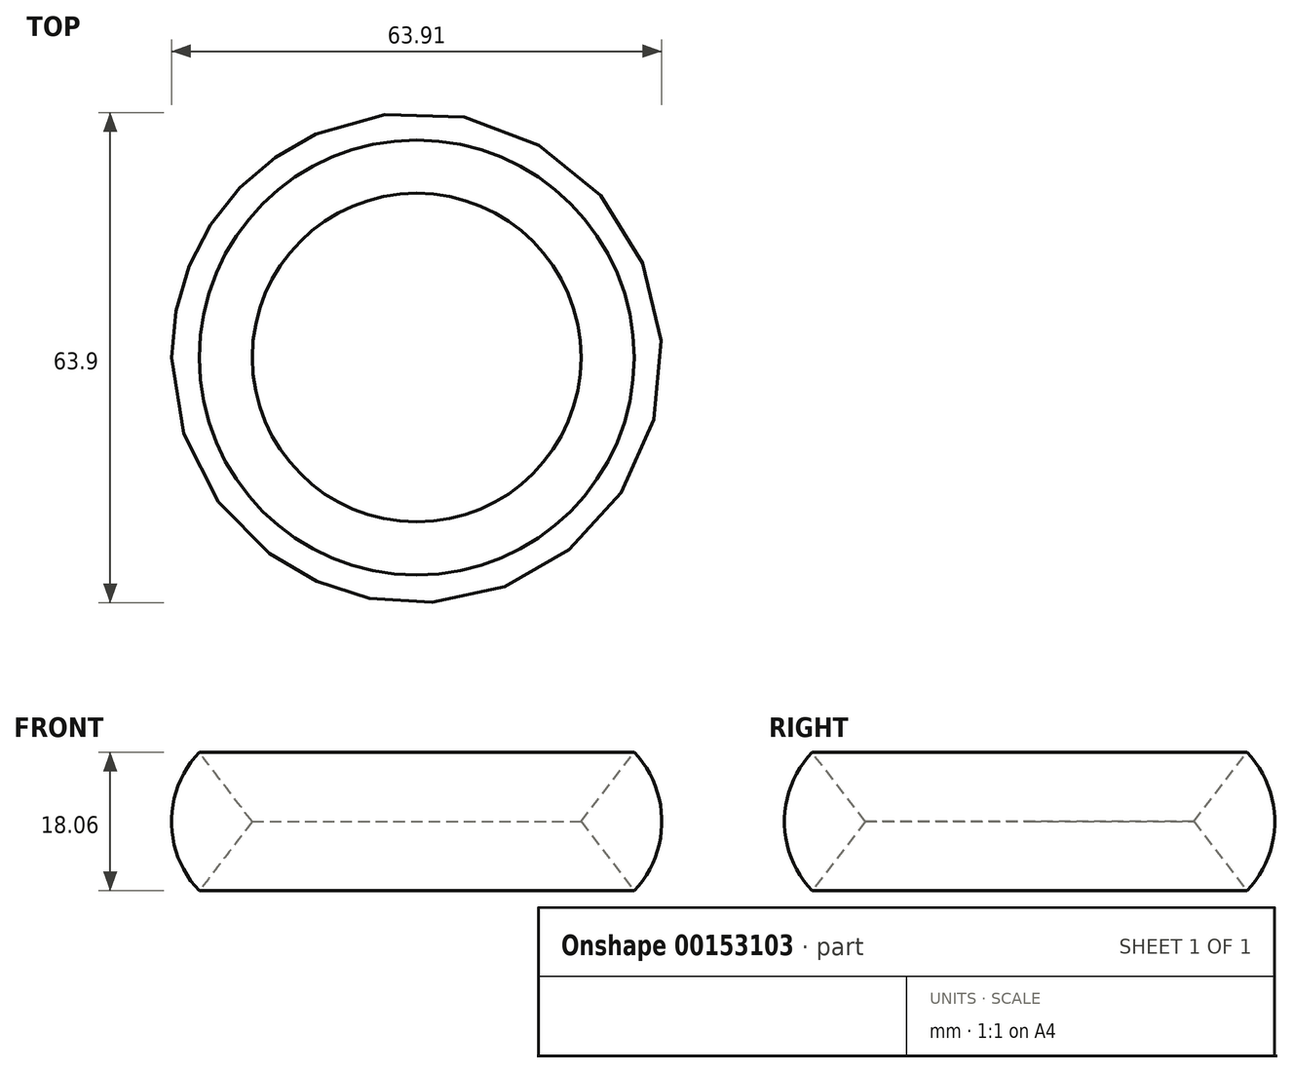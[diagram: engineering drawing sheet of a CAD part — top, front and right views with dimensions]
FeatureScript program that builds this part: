
annotation { "Feature Type Name" : "Feature", "Feature Type Description" : "" }
export const myFeature = defineFeature(function(context is Context, id is Id, definition is map)
    precondition{}
    {
        {
            var Q0;
            Q0=qCreatedBy(makeId("Front.planeOp"),FACE);
            var sketch = newSketch(context, id + "F0", { "sketchPlane" : qUnion([Q0])});
            skLineSegment(sketch, "E0", {"start": v(0, 0) * mm, "end": v(6.93, 9.03) * mm});
            skLineSegment(sketch, "E1", {"start": v(0, 0) * mm, "end": v(6.93, -9.03) * mm});
            skLineSegment(sketch, "E2", {"start": v(-21.42, 0) * mm, "end": v(-21.42, 22.5) * mm, "construction": true});
            skArc(sketch, "E3", {"start": v(6.93, -9.03) * mm, "mid": v(10.53, 0) * mm, "end": v(6.93, 9.03) * mm});
            skSolve(sketch);
        }
        {
            var Q0;
            Q0=makeQuery(id+"F0.imprint","IMPRINT",FACE,{"disambiguationData":[TD([[makeQuery(id+"F0.imprint","IMPRINT",EDGE,{"derivedFrom":sQuery(id+"F0.wireOp",EDGE,"E0")}),-1.0]])]});
            var Q1;
            Q1=sQuery(id+"F0.wireOp",EDGE,"E2");
            revolve(context, id + "F1", {"entities" : qUnion([Q0]), "axis" : qUnion([Q1]), "revolveType" : RevolveType.FULL});
        }
    });
